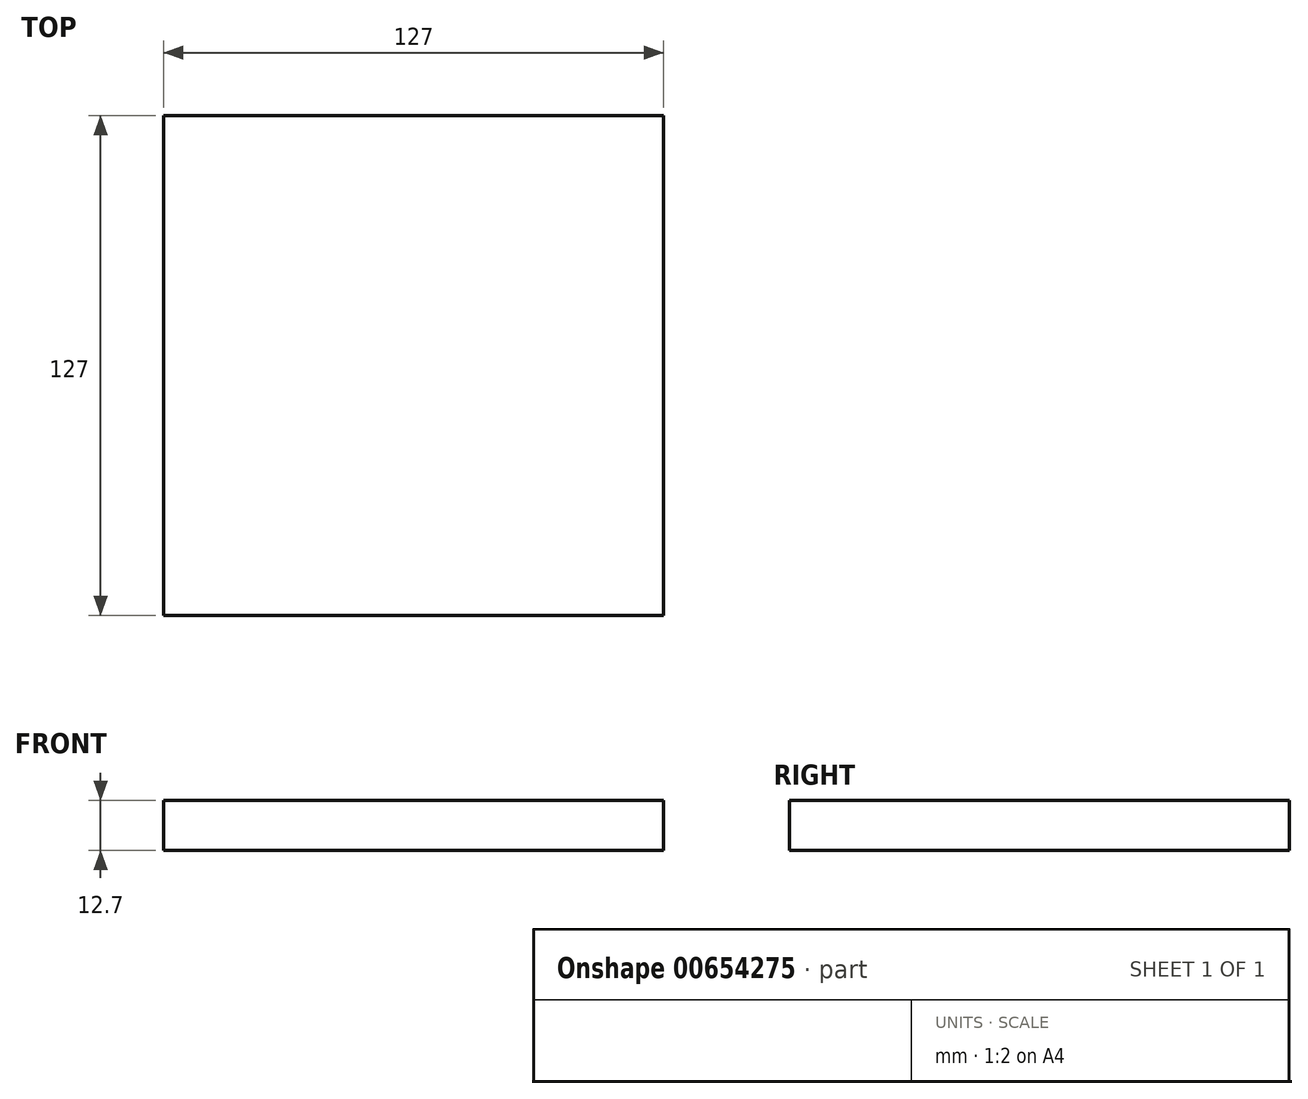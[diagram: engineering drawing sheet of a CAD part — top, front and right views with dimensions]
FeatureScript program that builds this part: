
annotation { "Feature Type Name" : "Feature", "Feature Type Description" : "" }
export const myFeature = defineFeature(function(context is Context, id is Id, definition is map)
    precondition{}
    {
        {
            var Q0;
            Q0=qCreatedBy(makeId("Top.planeOp"),FACE);
            var sketch = newSketch(context, id + "F0", { "sketchPlane" : qUnion([Q0])});
            skLineSegment(sketch, "E0.bottom", {"start": v(-63.5, 63.5) * mm, "end": v(63.5, 63.5) * mm});
            skLineSegment(sketch, "E0.top", {"start": v(-63.5, -63.5) * mm, "end": v(63.5, -63.5) * mm});
            skLineSegment(sketch, "E0.left", {"start": v(-63.5, 63.5) * mm, "end": v(-63.5, -63.5) * mm});
            skLineSegment(sketch, "E0.right", {"start": v(63.5, 63.5) * mm, "end": v(63.5, -63.5) * mm});
            skPoint(sketch, "E0.middle", {"position": v(0, 0) * mm});
            skSolve(sketch);
        }
        {
            var Q0;
            Q0=makeQuery(id+"F0.imprint","IMPRINT",FACE,{"disambiguationData":[TD([[makeQuery(id+"F0.imprint","IMPRINT",EDGE,{"derivedFrom":sQuery(id+"F0.wireOp",EDGE,"E0.bottom")}),-1.0]])]});
            extrude(context, id + "F1", {"entities" : qUnion([Q0]), "oppositeDirection" : true, "depth" : 12.7 * mm, "offsetDistance" : 25.4 * mm});
        }
    });
